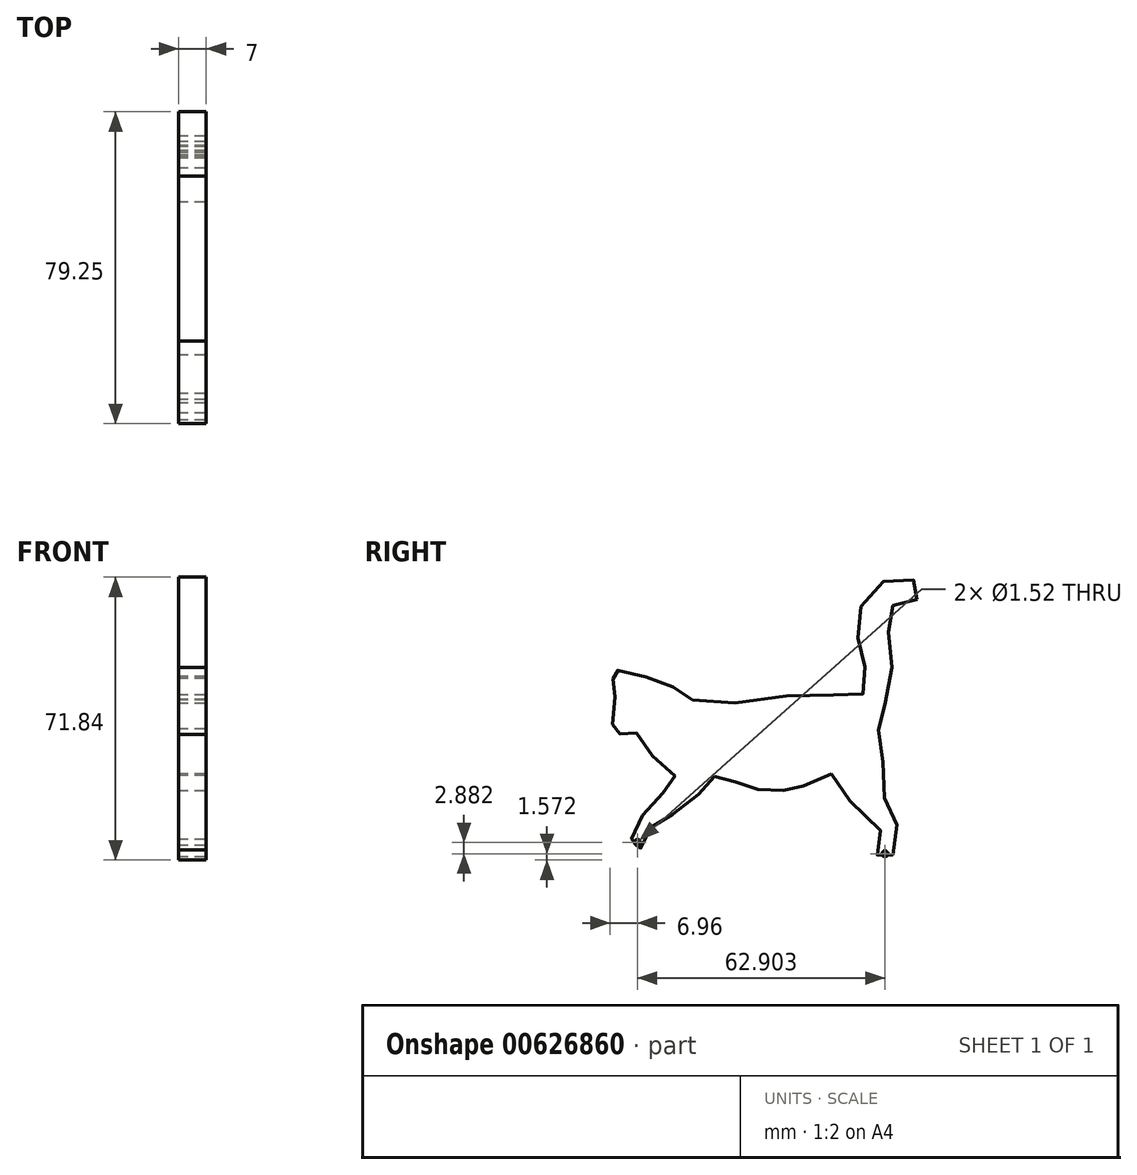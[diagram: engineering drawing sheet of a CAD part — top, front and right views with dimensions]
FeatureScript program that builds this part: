
annotation { "Feature Type Name" : "Feature", "Feature Type Description" : "" }
export const myFeature = defineFeature(function(context is Context, id is Id, definition is map)
    precondition{}
    {
        {
            var Q0;
            Q0=qCreatedBy(makeId("Right.planeOp"),FACE);
            var sketch = newSketch(context, id + "F0", { "sketchPlane" : qUnion([Q0])});
            skLineSegment(sketch, "E0.bottom", {"start": v(35.23, 45.45) * mm, "end": v(-44.77, 45.45) * mm});
            skLineSegment(sketch, "E0.top", {"start": v(35.23, -34.55) * mm, "end": v(-44.77, -34.55) * mm});
            skLineSegment(sketch, "E0.left", {"start": v(35.23, 45.45) * mm, "end": v(35.23, -34.55) * mm});
            skLineSegment(sketch, "E0.right", {"start": v(-44.77, 45.45) * mm, "end": v(-44.77, -34.55) * mm});
            skSolve(sketch);
        }
        {
            var Q0;
            Q0=makeQuery(id+"F0.imprint","IMPRINT",FACE,{"disambiguationData":[TD([[makeQuery(id+"F0.imprint","IMPRINT",EDGE,{"derivedFrom":sQuery(id+"F0.wireOp",EDGE,"E0.bottom")}),1.0]])]});
            var sketch = newSketch(context, id + "F1", { "sketchPlane" : qUnion([Q0])});
            skFitSpline(sketch, "E1", {"points": [v(-23.31, 13.68) * mm, v(-25.01, 14.32) * mm, v(-27.48, 16.19) * mm, v(-30.28, 18.44) * mm, v(-34.45, 19.6) * mm, v(-37.6, 19.08) * mm, v(-42.1, 21.12) * mm, v(-44.23, 21.89) * mm, v(-44.23, 21.63) * mm, v(-43.8, 19.5) * mm, v(-41.55, 16.49) * mm, v(-41.98, 15.9) * mm, v(-43.17, 13.9) * mm, v(-43.34, 10.32) * mm, v(-43.76, 7.22) * mm, v(-44.06, 6.75) * mm, v(-43.76, 6.15) * mm, v(-42.66, 5.39) * mm, v(-40.91, 5) * mm, v(-38.7, 6.24) * mm, v(-38.1, 5.86) * mm, v(-37.05, 4.67) * mm, v(-34.5, 0.97) * mm, v(-32.7, -1.63) * mm, v(-29.43, -4.94) * mm, v(-26.88, -6.22) * mm, v(-27.86, -7.37) * mm, v(-32.03, -11.24) * mm, v(-35, -14.51) * mm, v(-36.66, -16.68) * mm, v(-37.98, -19.53) * mm, v(-38.96, -22.5) * mm, v(-38.58, -23.82) * mm, v(-37.51, -24.42) * mm, v(-36.2, -23.78) * mm, v(-35.22, -21.74) * mm, v(-33.9, -18.8) * mm, v(-32.62, -17.57) * mm, v(-29.86, -16.25) * mm, v(-25.27, -13.4) * mm, v(-21.7, -10.26) * mm, v(-19.65, -7.62) * mm, v(-18.17, -6.05) * mm, v(-16.3, -5.58) * mm, v(-14.04, -6.18) * mm, v(-12.09, -7.37) * mm, v(-10.98, -8.05) * mm, v(-7.45, -8.94) * mm, v(-3.58, -9.4) * mm, v(-0.86, -9.37) * mm, v(1.6, -9.03) * mm, v(4.03, -8.35) * mm, v(4.62, -8.22) * mm, v(7.22, -7.45) * mm, v(12.02, -5.16) * mm], "startDerivative": vector(-103.94, 29.5) * mm, "endDerivative": vector(232.3, 145.86) * mm});
            skFitSpline(sketch, "E2", {"points": [v(12.02, -5.16) * mm, v(12.83, -6.52) * mm, v(15.5, -10.56) * mm, v(19.5, -15.02) * mm, v(24.35, -19.4) * mm, v(24.57, -20.08) * mm, v(24.52, -24.04) * mm, v(23.72, -25.52) * mm, v(23.67, -26.46) * mm, v(24.23, -26.84) * mm, v(25.93, -26.93) * mm, v(27.63, -25.65) * mm, v(28.52, -23.61) * mm, v(28.82, -19.49) * mm, v(28.1, -15.96) * mm, v(26.82, -13.4) * mm, v(25.03, -10.26) * mm, v(24.95, -5.62) * mm, v(24.95, -0.7) * mm, v(23.93, 4.16) * mm, v(23.93, 5.77) * mm, v(23.3, 9.05) * mm, v(24.4, 10.66) * mm, v(26.14, 13.8) * mm, v(27.29, 18.06) * mm, v(27.2, 24.9) * mm, v(26.7, 28.82) * mm, v(26.31, 32.47) * mm, v(26.31, 35.7) * mm, v(27.37, 37.4) * mm, v(28.48, 38.04) * mm, v(30.69, 38.47) * mm, v(33.28, 38.9) * mm, v(34.81, 40.51) * mm, v(34.86, 41.96) * mm, v(33.28, 43.83) * mm, v(30.73, 44.8) * mm, v(26.95, 44.34) * mm, v(23.67, 42.93) * mm, v(20.95, 40.34) * mm, v(19, 35.58) * mm, v(18.66, 32.56) * mm, v(18.83, 29.07) * mm, v(19.89, 25) * mm, v(20.4, 23.12) * mm, v(20.65, 19.85) * mm, v(20.61, 17.3) * mm, v(20.06, 15.3) * mm, v(18.1, 13.85) * mm, v(14.91, 14.57) * mm, v(7.35, 14.96) * mm, v(0, 14.66) * mm, v(-9.62, 13.21) * mm, v(-18.3, 12.83) * mm, v(-23.31, 13.68) * mm], "startDerivative": vector(52.7, -90.97) * mm, "endDerivative": vector(-203.25, 46.02) * mm});
            skSolve(sketch);
        }
        {
            var Q0;
            Q0=makeQuery(id+"F1.imprint","IMPRINT",FACE,{"disambiguationData":[TD([[makeQuery(id+"F1.imprint","IMPRINT",EDGE,{"derivedFrom":sQuery(id+"F1.wireOp",EDGE,"E1")}),1.0]])]});
            extrude(context, id + "F2", {"entities" : qUnion([Q0]), "depth" : 7 * mm, "offsetDistance" : 25 * mm});
        }
        {
            var Q0;
            Q0=qCreatedBy(makeId("Right.planeOp"),FACE);
            var sketch = newSketch(context, id + "F3", { "sketchPlane" : qUnion([Q0])});
            skCircle(sketch, "E3", {"center": v(-37.3, -22.56) * mm, "radius": 0.76 * mm});
            skCircle(sketch, "E4", {"center": v(25.6, -25.44) * mm, "radius": 0.76 * mm});
            skSolve(sketch);
        }
        {
            var Q0;
            Q0=makeQuery(id+"F3.imprint","IMPRINT",FACE,{"disambiguationData":[TD([[makeQuery(id+"F3.imprint","IMPRINT",EDGE,{"derivedFrom":sQuery(id+"F3.wireOp",EDGE,"E3")}),1.0]])]});
            var Q1;
            Q1=makeQuery(id+"F3.imprint","IMPRINT",FACE,{"disambiguationData":[TD([[makeQuery(id+"F3.imprint","IMPRINT",EDGE,{"derivedFrom":sQuery(id+"F3.wireOp",EDGE,"E4")}),1.0]])]});
            var Q2;
            Q2=sQuery(id+"F3.wireOp",EDGE,"E3");
            var Q3;
            Q3=sQuery(id+"F3.wireOp",EDGE,"E4");
            extrude(context, id + "F4", {"entities" : qUnion([Q0, Q1]), "operationType" : NewBodyOperationType.REMOVE, "surfaceEntities" : qUnion([Q2, Q3]), "depth" : 25 * mm, "offsetDistance" : 25 * mm});
        }
    });
